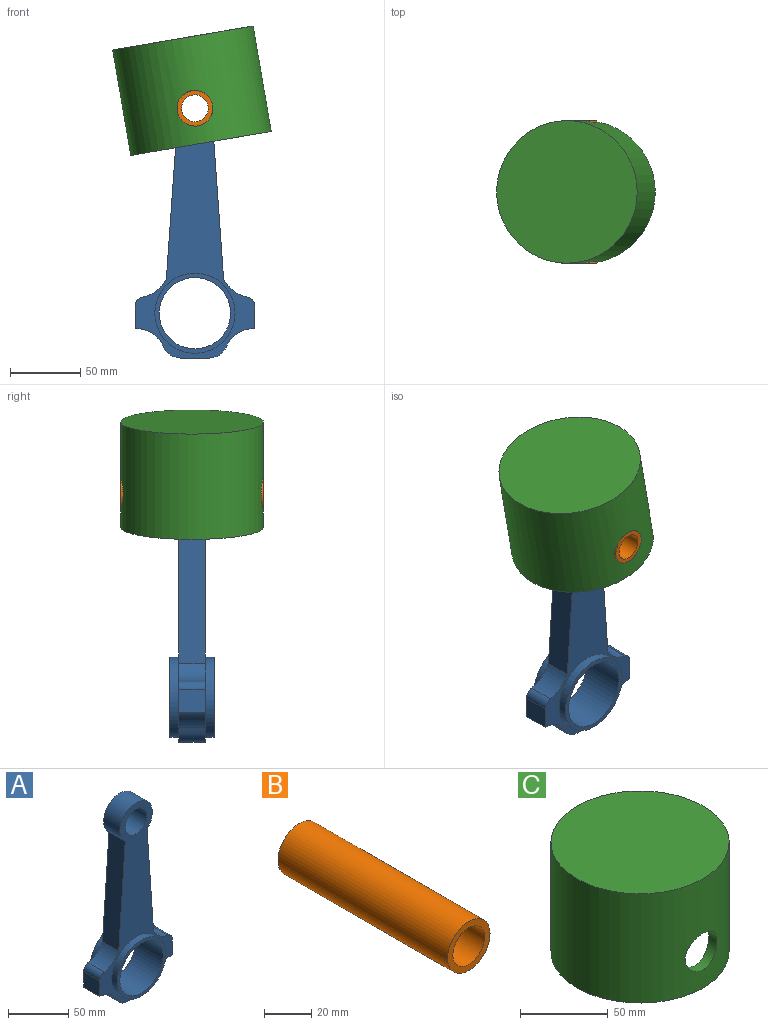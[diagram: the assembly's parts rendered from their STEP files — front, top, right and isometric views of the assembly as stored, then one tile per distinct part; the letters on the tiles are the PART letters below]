
ASSEMBLY  parts=3 mates=2
PART A: 22 faces, bbox 85.1x31.8x197 mm
  f0: plane 107.62x19.05mm, normal (1,0,0.07), area 2055.3mm2, adj f1,f10,f11,f12
  f1: cylinder r=19.05mm len=38.1mm, axis (0,1,0), area 1745.4mm2, adj f0,f2,f11,f12
  f2: plane 107.62x19.05mm, normal (-1,0,0.07), area 2055.3mm2, adj f1,f3,f11,f12
  f3: cylinder r=24.91mm len=19.05mm, axis (0,1,0), area 421.8mm2, adj f2,f11,f12,f20
  f4: plane 19.05x16.02mm, normal (-1,0,0), area 305.2mm2, adj f5,f11,f12,f20
  f5: cylinder r=22.15mm len=20.35mm, axis (0,1,0), area 491.5mm2, adj f4,f11,f12,f18
  f6: plane 21.04x19.05mm, normal (0,0,-1), area 400.7mm2, adj f11,f12,f18,f19
  f7: cylinder r=22.15mm len=20.35mm, axis (0,1,0), area 491.5mm2, adj f8,f11,f12,f19
  f8: plane 19.05x16.02mm, normal (1,0,0), area 305.2mm2, adj f7,f11,f12,f21
  f9: cylinder r=12.7mm len=25.4mm, axis (0,1,0), area 1520.1mm2, adj f11,f12
  f10: cylinder r=24.91mm len=19.05mm, axis (0,1,0), area 421.8mm2, adj f0,f11,f12,f21
  f11: plane 197.04x85.07mm, normal (0,-1,0), area 5148mm2, adj f0,f1,f2,f3,f4,f5,f6,f7
  f12: plane 197.04x85.07mm, normal (0,1,0), area 5148mm2, adj f0,f1,f2,f3,f4,f5,f6,f7
  f13: cylinder r=28.57mm len=57.15mm, axis (0,1,0), area 1140.1mm2, adj f11,f15
  f14: cylinder r=25.4mm len=50.8mm, axis (0,1,0), area 5067.1mm2, adj f15,f17
  f15: plane 57.15x57.15mm, normal (0,-1,0), area 538.4mm2, adj f13,f14
  f16: cylinder r=28.57mm len=57.15mm, axis (0,-1,0), area 1140.1mm2, adj f12,f17
  f17: plane 57.15x57.15mm, normal (0,1,0), area 538.4mm2, adj f14,f16
  f18: cylinder r=12.7mm len=19.05mm, axis (0,1,0), area 281.8mm2, adj f5,f6,f11,f12
  f19: cylinder r=12.7mm len=19.05mm, axis (0,1,0), area 281.8mm2, adj f6,f7,f11,f12
  f20: cylinder r=6.35mm len=19.05mm, axis (0,1,0), area 165.3mm2, adj f3,f4,f11,f12
  f21: cylinder r=6.35mm len=19.05mm, axis (0,1,0), area 165.3mm2, adj f8,f10,f11,f12
PART B: 4 faces, bbox 25.4x101.6x25.4 mm
  f0: cylinder r=9.53mm len=101.6mm, axis (0,1,0), area 6080.5mm2, adj f2,f3
  f1: cylinder r=12.7mm len=101.6mm, axis (0,1,0), area 8107.3mm2, adj f2,f3
  f2: plane 25.4x25.4mm, normal (0,-1,0), area 221.7mm2, adj f0,f1
  f3: plane 25.4x25.4mm, normal (0,1,0), area 221.7mm2, adj f0,f1
PART C: 7 faces, bbox 101.6x101.6x76.2 mm
  f0: cylinder r=44.45mm len=88.9mm, axis (0,0,-1), area 16709.8mm2, adj f3,f4,f5,f6
  f1: cylinder r=50.8mm len=101.6mm, axis (0,0,-1), area 23298mm2, adj f2,f3,f5,f6
  f2: plane 101.6x101.6mm, normal (0,0,1), area 8107.3mm2, adj f1
  f3: plane 101.6x101.6mm, normal (0,0,-1), area 1900.2mm2, adj f0,f1
  f4: plane 88.9x88.9mm, normal (0,0,-1), area 6207.2mm2, adj f0
  f5: cylinder r=12.7mm len=25.4mm, axis (0,-1,0), area 516.2mm2, adj f0,f1
  f6: cylinder r=12.7mm len=25.4mm, axis (0,-1,0), area 516.2mm2, adj f0,f1
PLACE A t=(30.89,-17.29,-9.84)mm fixed
PLACE B t=(30.89,-26.81,136.21)mm
PLACE C rot(axis=(0,-1,0),9.7deg) t=(35.18,-26.88,111.17)mm
MATE revolute C.f5 <-> B.f0  axis (0,-1,0) through (30.89,23.99,136.21)mm
MATE fastened B.f0 <-> A.f1  axis (0,1,0) through (30.89,-26.81,136.21)mm
